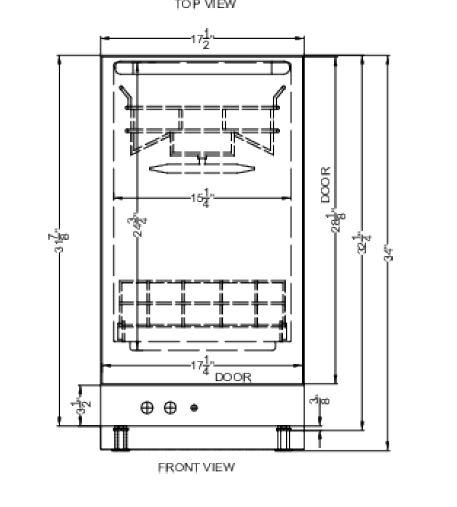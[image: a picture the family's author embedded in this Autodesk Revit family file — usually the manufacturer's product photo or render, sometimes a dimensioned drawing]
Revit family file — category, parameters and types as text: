
# Revit family: QF_Summit_DW186NTADA_Dishwasher
name_source: partatom
category: Specialty Equipment
units: mm (PartAtom-declared; Revit-internal decimal feet)

## family parameters
Always vertical = Yes
Cut with Voids When Loaded = No
Part Type = Normal
Room Calculation Point = No
Round Connector Dimension = Use Diameter
Shared = No
Work Plane-Based = No

## types (1)
- QF_Summit_DW186NTADA_Dishwasher
    Apparent Power = 1380 VA
    Cold Water Connection Height = 0"
    Cold Water Flow = 0 GPM
    Cold Water Maximum Pressure = 0.00 psi
    Cold Water Minimum Pressure = 0.00 psi
    Cold Water RI Height = 0"
    Cold Water Size = 1"
    Cold Water Temperature Recommended = -460 °F
    Conn Conduit = Yes
    Cycle = 60 Hz
    Default Elevation = 0"
    Depth = 21 5/8"
    Description = Dishwasher
    Elec Conn Connection Height = 0"
    Elec Conn RI Height = 0"
    FL Amps = 12 A
    Foodservice Equipment Identifier = Yes
    Identify Quantity as Lot = Yes
    Indirect Waste Connection Height = 0"
    Indirect Waste Flow = 0 GPM
    Indirect Waste Size = 1"
    Length = 17 1/2"
    Manufacturer = Summit
    Max Overcurrent Protection = 0 A
    Min Ckt Ampacity = 0 A
    Model = DW186NTADA
    Number of Poles = 1
    Phase = 1
    Volts = 115 V
    Waste Water Discharge Temperature = -460 °F
    Watts = 1380 W
    Weight in Pounds = 95

## geometry (parser evidence)
native form markers: Blend x2, Sweep x9
no freeform markers — native parametric forms only
